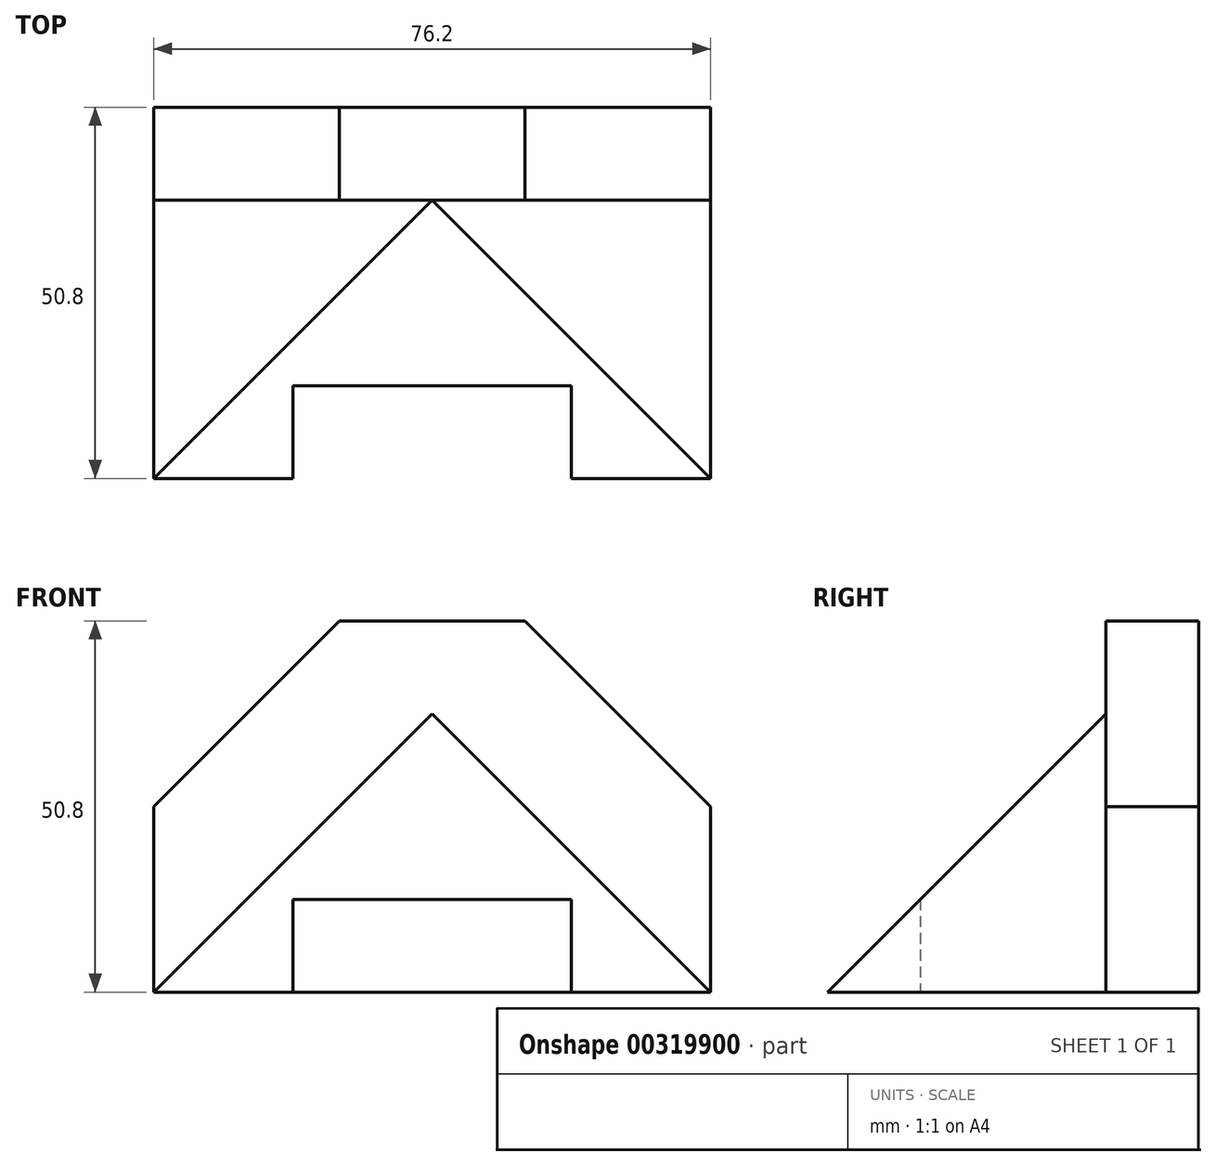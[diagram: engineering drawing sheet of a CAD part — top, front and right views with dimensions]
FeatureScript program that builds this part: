
annotation { "Feature Type Name" : "Feature", "Feature Type Description" : "" }
export const myFeature = defineFeature(function(context is Context, id is Id, definition is map)
    precondition{}
    {
        {
            var Q0;
            Q0=qCreatedBy(makeId("Right.planeOp"),FACE);
            var sketch = newSketch(context, id + "F0", { "sketchPlane" : qUnion([Q0])});
            skLineSegment(sketch, "E0", {"start": v(0, 0) * mm, "end": v(38.1, 0) * mm});
            skLineSegment(sketch, "E1", {"start": v(38.1, 0) * mm, "end": v(38.1, 38.1) * mm});
            skLineSegment(sketch, "E2", {"start": v(38.1, 38.1) * mm, "end": v(0, 0) * mm});
            skLineSegment(sketch, "E3", {"start": v(38.1, 0) * mm, "end": v(50.8, 0) * mm});
            skLineSegment(sketch, "E4", {"start": v(50.8, 0) * mm, "end": v(50.8, 50.8) * mm});
            skLineSegment(sketch, "E5", {"start": v(50.8, 50.8) * mm, "end": v(38.1, 50.8) * mm});
            skLineSegment(sketch, "E6", {"start": v(38.1, 50.8) * mm, "end": v(38.1, 0) * mm});
            skSolve(sketch);
        }
        {
            var Q0;
            {var subQ3=sQuery(id+"F0.wireOp",EDGE,"E3");Q0=makeQuery(id+"F0.imprint","IMPRINT",FACE,{"disambiguationData":[TD([[makeQuery(id+"F0.imprint","IMPRINT",EDGE,{"derivedFrom":subQ3}),1.0]])]});}
            var Q1;
            {var subQ0=sQuery(id+"F0.wireOp",EDGE,"E0");Q1=makeQuery(id+"F0.imprint","IMPRINT",FACE,{"disambiguationData":[TD([[makeQuery(id+"F0.imprint","IMPRINT",EDGE,{"derivedFrom":subQ0}),1.0]])]});}
            extrude(context, id + "F1", {"entities" : qUnion([Q0, Q1]), "depth" : 76.2 * mm});
        }
        {
            var Q0;
            Q0=makeQuery(id+"F1.opExtrude","SWEPT_FACE",FACE,{"disambiguationData":[OSD([sQuery(id+"F0.wireOp",EDGE,"E4")])]});
            var sketch = newSketch(context, id + "F2", { "sketchPlane" : qUnion([Q0])});
            skLineSegment(sketch, "E7", {"start": v(0, 0) * mm, "end": v(-76.2, 0) * mm});
            skLineSegment(sketch, "E8", {"start": v(-76.2, 0) * mm, "end": v(-38.1, 38.1) * mm});
            skLineSegment(sketch, "E9", {"start": v(0, 0) * mm, "end": v(-38.1, 38.1) * mm});
            skSolve(sketch);
        }
        {
            var Q0;
            Q0=makeQuery(id+"F2.imprint","IMPRINT",FACE,{"disambiguationData":[TD([[makeQuery(id+"F2.imprint","IMPRINT",EDGE,{"derivedFrom":sQuery(id+"F2.wireOp",EDGE,"E8")}),1.0]])]});
            extrude(context, id + "F3", {"entities" : qUnion([Q0]), "operationType" : NewBodyOperationType.REMOVE, "oppositeDirection" : true, "depth" : 50.8 * mm, "hasSecondDirection" : true, "secondDirectionOppositeDirection" : true, "secondDirectionDepth" : 12.7 * mm});
        }
        {
            var Q0;
            Q0=makeQuery(id+"F3.boolean.opBoolean","MERGE",FACE,{"derivedFrom":[makeQuery(id+"F1.opExtrude","SWEPT_FACE",FACE,{"disambiguationData":[OSD([sQuery(id+"F0.wireOp",EDGE,"E6")])]}),makeQuery(id+"F3.opExtrude","CAP_FACE",FACE,{"disambiguationData":[OSD([sQuery(id+"F0.wireOp",EDGE,"E4"),sQuery(id+"F0.wireOp",EDGE,"E5"),sQuery(id+"F2.wireOp",EDGE,"E8"),sQuery(id+"F2.wireOp",EDGE,"E9")])],"isStart":true})]});
            var sketch = newSketch(context, id + "F4", { "sketchPlane" : qUnion([Q0])});
            skLineSegment(sketch, "E10", {"start": v(0, 50.8) * mm, "end": v(25.4, 50.8) * mm});
            skLineSegment(sketch, "E11", {"start": v(0, 50.8) * mm, "end": v(0, 25.4) * mm});
            skLineSegment(sketch, "E12", {"start": v(0, 25.4) * mm, "end": v(25.4, 50.8) * mm});
            skLineSegment(sketch, "E13", {"start": v(76.2, 50.8) * mm, "end": v(76.2, 25.4) * mm});
            skLineSegment(sketch, "E14", {"start": v(76.2, 25.4) * mm, "end": v(50.8, 50.8) * mm});
            skLineSegment(sketch, "E15", {"start": v(50.8, 50.8) * mm, "end": v(76.2, 50.8) * mm});
            skSolve(sketch);
        }
        {
            var Q0;
            Q0=makeQuery(id+"F4.imprint","IMPRINT",FACE,{"disambiguationData":[TD([[makeQuery(id+"F4.imprint","IMPRINT",EDGE,{"derivedFrom":sQuery(id+"F4.wireOp",EDGE,"E10")}),1.0]])]});
            var Q1;
            Q1=makeQuery(id+"F4.imprint","IMPRINT",FACE,{"disambiguationData":[TD([[makeQuery(id+"F4.imprint","IMPRINT",EDGE,{"derivedFrom":sQuery(id+"F4.wireOp",EDGE,"E13")}),-1.0]])]});
            extrude(context, id + "F5", {"entities" : qUnion([Q0, Q1]), "operationType" : NewBodyOperationType.REMOVE, "oppositeDirection" : true, "depth" : 25.4 * mm});
        }
        {
            var Q0;
            Q0=makeQuery(id+"F1.opExtrude","SWEPT_FACE",FACE,{"disambiguationData":[OSD([sQuery(id+"F0.wireOp",EDGE,"E0"),sQuery(id+"F0.wireOp",EDGE,"E3")])]});
            var sketch = newSketch(context, id + "F6", { "sketchPlane" : qUnion([Q0])});
            skLineSegment(sketch, "E16", {"start": v(19.05, 0) * mm, "end": v(19.05, -12.7) * mm});
            skLineSegment(sketch, "E17", {"start": v(19.05, -12.7) * mm, "end": v(57.15, -12.7) * mm});
            skLineSegment(sketch, "E18", {"start": v(57.15, -12.7) * mm, "end": v(57.15, 0) * mm});
            skLineSegment(sketch, "E19", {"start": v(57.15, 0) * mm, "end": v(19.05, 0) * mm});
            skSolve(sketch);
        }
        {
            var Q0;
            Q0=makeQuery(id+"F6.imprint","IMPRINT",FACE,{"disambiguationData":[TD([[makeQuery(id+"F6.imprint","IMPRINT",EDGE,{"derivedFrom":sQuery(id+"F6.wireOp",EDGE,"E16")}),1.0]])]});
            extrude(context, id + "F7", {"entities" : qUnion([Q0]), "operationType" : NewBodyOperationType.REMOVE, "oppositeDirection" : true, "depth" : 25.4 * mm});
        }
    });
